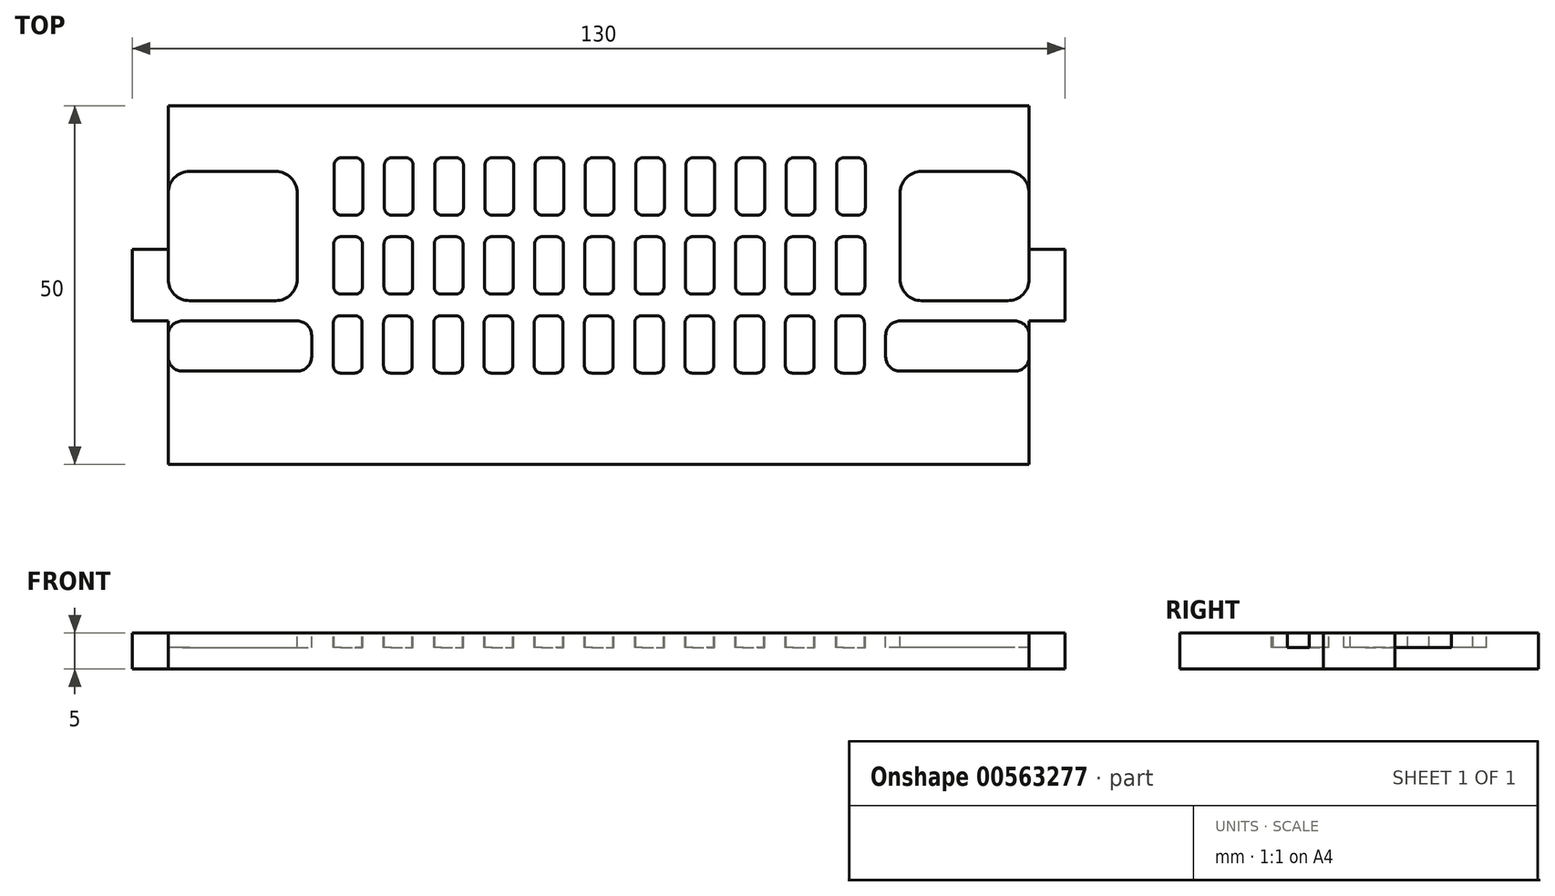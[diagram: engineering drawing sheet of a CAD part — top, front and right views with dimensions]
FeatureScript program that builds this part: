
annotation { "Feature Type Name" : "Feature", "Feature Type Description" : "" }
export const myFeature = defineFeature(function(context is Context, id is Id, definition is map)
    precondition{}
    {
        {
            var Q0;
            Q0=qCreatedBy(makeId("Top.planeOp"),FACE);
            var sketch = newSketch(context, id + "F0", { "sketchPlane" : qUnion([Q0])});
            skLineSegment(sketch, "E0.bottom", {"start": v(0, 0) * mm, "end": v(120, 0) * mm});
            skLineSegment(sketch, "E0.top", {"start": v(0, 50) * mm, "end": v(120, 50) * mm});
            skLineSegment(sketch, "E0.left", {"start": v(0, 0) * mm, "end": v(0, 20) * mm});
            skLineSegment(sketch, "E0.right", {"start": v(120, 0) * mm, "end": v(120, 20) * mm});
            skLineSegment(sketch, "E1.bottom", {"start": v(0, 30) * mm, "end": v(-5, 30) * mm});
            skLineSegment(sketch, "E1.top", {"start": v(0, 20) * mm, "end": v(-5, 20) * mm});
            skLineSegment(sketch, "E1.right", {"start": v(-5, 30) * mm, "end": v(-5, 20) * mm});
            skLineSegment(sketch, "E2.bottom", {"start": v(120, 30) * mm, "end": v(125, 30) * mm});
            skLineSegment(sketch, "E2.top", {"start": v(120, 20) * mm, "end": v(125, 20) * mm});
            skLineSegment(sketch, "E2.right", {"start": v(125, 30) * mm, "end": v(125, 20) * mm});
            skLineSegment(sketch, "E3.trimOffspring", {"start": v(0, 30) * mm, "end": v(0, 50) * mm});
            skLineSegment(sketch, "E4.trimOffspring", {"start": v(120, 30) * mm, "end": v(120, 50) * mm});
            skSolve(sketch);
        }
        {
            var Q0;
            Q0 = qSketchRegion(id + "F0", true);
            extrude(context, id + "F1", {"entities" : qUnion([Q0]), "depth" : 5 * mm, "offsetDistance" : 25 * mm});
        }
        {
            var Q0;
            Q0=makeQuery(id+"F1.opExtrude","CAP_FACE",FACE,{"disambiguationData":[OSD([sQuery(id+"F0.wireOp",EDGE,"E0.bottom"),sQuery(id+"F0.wireOp",EDGE,"E0.top"),sQuery(id+"F0.wireOp",EDGE,"E0.left"),sQuery(id+"F0.wireOp",EDGE,"E0.right"),sQuery(id+"F0.wireOp",EDGE,"E1.bottom"),sQuery(id+"F0.wireOp",EDGE,"E1.top"),sQuery(id+"F0.wireOp",EDGE,"E1.right"),sQuery(id+"F0.wireOp",EDGE,"E2.bottom"),sQuery(id+"F0.wireOp",EDGE,"E2.top"),sQuery(id+"F0.wireOp",EDGE,"E2.right"),sQuery(id+"F0.wireOp",EDGE,"E3.trimOffspring"),sQuery(id+"F0.wireOp",EDGE,"E4.trimOffspring")])],"isStart":false});
            var sketch = newSketch(context, id + "F2", { "sketchPlane" : qUnion([Q0])});
            skLineSegment(sketch, "E5.bottom", {"start": v(3, 40.83) * mm, "end": v(15, 40.83) * mm});
            skLineSegment(sketch, "E5.top", {"start": v(3, 22.83) * mm, "end": v(15, 22.83) * mm});
            skLineSegment(sketch, "E5.left", {"start": v(0, 37.83) * mm, "end": v(0, 25.83) * mm});
            skLineSegment(sketch, "E5.right", {"start": v(18, 37.83) * mm, "end": v(18, 25.83) * mm});
            skLineSegment(sketch, "E6.bottom", {"start": v(117, 40.83) * mm, "end": v(105, 40.83) * mm});
            skLineSegment(sketch, "E6.top", {"start": v(117, 22.83) * mm, "end": v(105, 22.83) * mm});
            skLineSegment(sketch, "E6.left", {"start": v(120, 37.83) * mm, "end": v(120, 25.83) * mm});
            skLineSegment(sketch, "E6.right", {"start": v(102, 37.83) * mm, "end": v(102, 25.83) * mm});
            skPoint(sketch, "E7.visualSharp", {"position": v(0, 40.83) * mm});
            skArc(sketch, "E7.filletArc", {"start": v(3, 40.83) * mm, "mid": v(0.88, 39.95) * mm, "end": v(0, 37.83) * mm});
            skPoint(sketch, "E8.visualSharp", {"position": v(18, 40.83) * mm});
            skArc(sketch, "E8.filletArc", {"start": v(18, 37.83) * mm, "mid": v(17.12, 39.95) * mm, "end": v(15, 40.83) * mm});
            skPoint(sketch, "E9.visualSharp", {"position": v(0, 22.83) * mm});
            skArc(sketch, "E9.filletArc", {"start": v(0, 25.83) * mm, "mid": v(0.88, 23.7) * mm, "end": v(3, 22.83) * mm});
            skPoint(sketch, "E10.visualSharp", {"position": v(102, 22.83) * mm});
            skArc(sketch, "E10.filletArc", {"start": v(102, 25.83) * mm, "mid": v(102.88, 23.7) * mm, "end": v(105, 22.83) * mm});
            skPoint(sketch, "E11.visualSharp", {"position": v(120, 40.83) * mm});
            skArc(sketch, "E11.filletArc", {"start": v(120, 37.83) * mm, "mid": v(119.12, 39.95) * mm, "end": v(117, 40.83) * mm});
            skPoint(sketch, "E12.visualSharp", {"position": v(102, 40.83) * mm});
            skArc(sketch, "E12.filletArc", {"start": v(105, 40.83) * mm, "mid": v(102.88, 39.95) * mm, "end": v(102, 37.83) * mm});
            skPoint(sketch, "E13.visualSharp", {"position": v(18, 22.83) * mm});
            skArc(sketch, "E13.filletArc", {"start": v(15, 22.83) * mm, "mid": v(17.12, 23.7) * mm, "end": v(18, 25.83) * mm});
            skPoint(sketch, "E14.visualSharp", {"position": v(120, 22.83) * mm});
            skArc(sketch, "E14.filletArc", {"start": v(117, 22.83) * mm, "mid": v(119.12, 23.7) * mm, "end": v(120, 25.83) * mm});
            skLineSegment(sketch, "E15.bottom", {"start": v(2, 20) * mm, "end": v(18, 20) * mm});
            skLineSegment(sketch, "E15.top", {"start": v(2, 13) * mm, "end": v(18, 13) * mm});
            skLineSegment(sketch, "E15.left", {"start": v(0, 18) * mm, "end": v(0, 15) * mm});
            skLineSegment(sketch, "E15.right", {"start": v(20, 18) * mm, "end": v(20, 15) * mm});
            skLineSegment(sketch, "E16.bottom", {"start": v(118, 20) * mm, "end": v(102, 20) * mm});
            skLineSegment(sketch, "E16.top", {"start": v(118, 13) * mm, "end": v(102, 13) * mm});
            skLineSegment(sketch, "E16.left", {"start": v(120, 18) * mm, "end": v(120, 15) * mm});
            skLineSegment(sketch, "E16.right", {"start": v(100, 18) * mm, "end": v(100, 15) * mm});
            skPoint(sketch, "E17.visualSharp", {"position": v(20, 20) * mm});
            skArc(sketch, "E17.filletArc", {"start": v(20, 18) * mm, "mid": v(19.41, 19.41) * mm, "end": v(18, 20) * mm});
            skPoint(sketch, "E18.visualSharp", {"position": v(0, 20) * mm});
            skArc(sketch, "E18.filletArc", {"start": v(2, 20) * mm, "mid": v(0.59, 19.41) * mm, "end": v(0, 18) * mm});
            skPoint(sketch, "E19.visualSharp", {"position": v(20, 13) * mm});
            skArc(sketch, "E19.filletArc", {"start": v(18, 13) * mm, "mid": v(19.41, 13.59) * mm, "end": v(20, 15) * mm});
            skPoint(sketch, "E20.visualSharp", {"position": v(100, 13) * mm});
            skArc(sketch, "E20.filletArc", {"start": v(100, 15) * mm, "mid": v(100.59, 13.59) * mm, "end": v(102, 13) * mm});
            skPoint(sketch, "E21.visualSharp", {"position": v(120, 20) * mm});
            skArc(sketch, "E21.filletArc", {"start": v(120, 18) * mm, "mid": v(119.41, 19.41) * mm, "end": v(118, 20) * mm});
            skPoint(sketch, "E22.visualSharp", {"position": v(100, 20) * mm});
            skArc(sketch, "E22.filletArc", {"start": v(102, 20) * mm, "mid": v(100.59, 19.41) * mm, "end": v(100, 18) * mm});
            skPoint(sketch, "E23.visualSharp", {"position": v(120, 13) * mm});
            skArc(sketch, "E23.filletArc", {"start": v(118, 13) * mm, "mid": v(119.41, 13.59) * mm, "end": v(120, 15) * mm});
            skPoint(sketch, "E24.visualSharp", {"position": v(0, 13) * mm});
            skArc(sketch, "E24.filletArc", {"start": v(0, 15) * mm, "mid": v(0.59, 13.59) * mm, "end": v(2, 13) * mm});
            skLineSegment(sketch, "E25.bottom", {"start": v(24.15, 42.74) * mm, "end": v(26.15, 42.74) * mm});
            skLineSegment(sketch, "E25.top", {"start": v(24.15, 34.74) * mm, "end": v(26.15, 34.74) * mm});
            skLineSegment(sketch, "E25.left", {"start": v(23.15, 41.74) * mm, "end": v(23.15, 35.74) * mm});
            skLineSegment(sketch, "E25.right", {"start": v(27.15, 41.74) * mm, "end": v(27.15, 35.74) * mm});
            skPoint(sketch, "E26.visualSharp", {"position": v(27.15, 42.74) * mm});
            skArc(sketch, "E26.filletArc", {"start": v(27.15, 41.74) * mm, "mid": v(26.86, 42.45) * mm, "end": v(26.15, 42.74) * mm});
            skPoint(sketch, "E27.visualSharp", {"position": v(23.15, 42.74) * mm});
            skArc(sketch, "E27.filletArc", {"start": v(24.15, 42.74) * mm, "mid": v(23.44, 42.45) * mm, "end": v(23.15, 41.74) * mm});
            skPoint(sketch, "E28.visualSharp", {"position": v(27.15, 34.74) * mm});
            skArc(sketch, "E28.filletArc", {"start": v(26.15, 34.74) * mm, "mid": v(26.86, 35.03) * mm, "end": v(27.15, 35.74) * mm});
            skPoint(sketch, "E29.visualSharp", {"position": v(23.15, 34.74) * mm});
            skArc(sketch, "E29.filletArc", {"start": v(23.15, 35.74) * mm, "mid": v(23.44, 35.03) * mm, "end": v(24.15, 34.74) * mm});
            skLineSegment(sketch, "E30.direction1", {"start": v(23.15, 34.74) * mm, "end": v(26.15, 34.74) * mm, "construction": true});
            skLineSegment(sketch, "E31.1.0.0", {"start": v(31.15, 42.74) * mm, "end": v(33.15, 42.74) * mm});
            skPoint(sketch, "E31.1.0.1", {"position": v(34.15, 42.74) * mm});
            skLineSegment(sketch, "E31.1.0.2", {"start": v(30.15, 34.74) * mm, "end": v(33.15, 34.74) * mm, "construction": true});
            skPoint(sketch, "E31.1.0.3", {"position": v(30.15, 42.74) * mm});
            skLineSegment(sketch, "E31.1.0.4", {"start": v(34.15, 41.74) * mm, "end": v(34.15, 35.74) * mm});
            skLineSegment(sketch, "E31.1.0.5", {"start": v(30.15, 41.74) * mm, "end": v(30.15, 35.74) * mm});
            skPoint(sketch, "E31.1.0.6", {"position": v(30.15, 34.74) * mm});
            skPoint(sketch, "E31.1.0.7", {"position": v(34.15, 34.74) * mm});
            skArc(sketch, "E31.1.0.8", {"start": v(34.15, 41.74) * mm, "mid": v(33.86, 42.45) * mm, "end": v(33.15, 42.74) * mm});
            skArc(sketch, "E31.1.0.9", {"start": v(31.15, 42.74) * mm, "mid": v(30.44, 42.45) * mm, "end": v(30.15, 41.74) * mm});
            skArc(sketch, "E31.1.0.10", {"start": v(30.15, 35.74) * mm, "mid": v(30.44, 35.03) * mm, "end": v(31.15, 34.74) * mm});
            skArc(sketch, "E31.1.0.11", {"start": v(33.15, 34.74) * mm, "mid": v(33.86, 35.03) * mm, "end": v(34.15, 35.74) * mm});
            skLineSegment(sketch, "E31.1.0.12", {"start": v(31.15, 34.74) * mm, "end": v(33.15, 34.74) * mm});
            skLineSegment(sketch, "E31.2.0.0", {"start": v(38.15, 42.74) * mm, "end": v(40.15, 42.74) * mm});
            skPoint(sketch, "E31.2.0.1", {"position": v(41.15, 42.74) * mm});
            skLineSegment(sketch, "E31.2.0.2", {"start": v(37.15, 34.74) * mm, "end": v(40.15, 34.74) * mm, "construction": true});
            skPoint(sketch, "E31.2.0.3", {"position": v(37.15, 42.74) * mm});
            skLineSegment(sketch, "E31.2.0.4", {"start": v(41.15, 41.74) * mm, "end": v(41.15, 35.74) * mm});
            skLineSegment(sketch, "E31.2.0.5", {"start": v(37.15, 41.74) * mm, "end": v(37.15, 35.74) * mm});
            skPoint(sketch, "E31.2.0.6", {"position": v(37.15, 34.74) * mm});
            skPoint(sketch, "E31.2.0.7", {"position": v(41.15, 34.74) * mm});
            skArc(sketch, "E31.2.0.8", {"start": v(41.15, 41.74) * mm, "mid": v(40.86, 42.45) * mm, "end": v(40.15, 42.74) * mm});
            skArc(sketch, "E31.2.0.9", {"start": v(38.15, 42.74) * mm, "mid": v(37.44, 42.45) * mm, "end": v(37.15, 41.74) * mm});
            skArc(sketch, "E31.2.0.10", {"start": v(37.15, 35.74) * mm, "mid": v(37.44, 35.03) * mm, "end": v(38.15, 34.74) * mm});
            skArc(sketch, "E31.2.0.11", {"start": v(40.15, 34.74) * mm, "mid": v(40.86, 35.03) * mm, "end": v(41.15, 35.74) * mm});
            skLineSegment(sketch, "E31.2.0.12", {"start": v(38.15, 34.74) * mm, "end": v(40.15, 34.74) * mm});
            skLineSegment(sketch, "E31.3.0.0", {"start": v(45.15, 42.74) * mm, "end": v(47.15, 42.74) * mm});
            skPoint(sketch, "E31.3.0.1", {"position": v(48.15, 42.74) * mm});
            skLineSegment(sketch, "E31.3.0.2", {"start": v(44.15, 34.74) * mm, "end": v(47.15, 34.74) * mm, "construction": true});
            skPoint(sketch, "E31.3.0.3", {"position": v(44.15, 42.74) * mm});
            skLineSegment(sketch, "E31.3.0.4", {"start": v(48.15, 41.74) * mm, "end": v(48.15, 35.74) * mm});
            skLineSegment(sketch, "E31.3.0.5", {"start": v(44.15, 41.74) * mm, "end": v(44.15, 35.74) * mm});
            skPoint(sketch, "E31.3.0.6", {"position": v(44.15, 34.74) * mm});
            skPoint(sketch, "E31.3.0.7", {"position": v(48.15, 34.74) * mm});
            skArc(sketch, "E31.3.0.8", {"start": v(48.15, 41.74) * mm, "mid": v(47.86, 42.45) * mm, "end": v(47.15, 42.74) * mm});
            skArc(sketch, "E31.3.0.9", {"start": v(45.15, 42.74) * mm, "mid": v(44.44, 42.45) * mm, "end": v(44.15, 41.74) * mm});
            skArc(sketch, "E31.3.0.10", {"start": v(44.15, 35.74) * mm, "mid": v(44.44, 35.03) * mm, "end": v(45.15, 34.74) * mm});
            skArc(sketch, "E31.3.0.11", {"start": v(47.15, 34.74) * mm, "mid": v(47.86, 35.03) * mm, "end": v(48.15, 35.74) * mm});
            skLineSegment(sketch, "E31.3.0.12", {"start": v(45.15, 34.74) * mm, "end": v(47.15, 34.74) * mm});
            skLineSegment(sketch, "E31.4.0.0", {"start": v(52.15, 42.74) * mm, "end": v(54.15, 42.74) * mm});
            skPoint(sketch, "E31.4.0.1", {"position": v(55.15, 42.74) * mm});
            skLineSegment(sketch, "E31.4.0.2", {"start": v(51.15, 34.74) * mm, "end": v(54.15, 34.74) * mm, "construction": true});
            skPoint(sketch, "E31.4.0.3", {"position": v(51.15, 42.74) * mm});
            skLineSegment(sketch, "E31.4.0.4", {"start": v(55.15, 41.74) * mm, "end": v(55.15, 35.74) * mm});
            skLineSegment(sketch, "E31.4.0.5", {"start": v(51.15, 41.74) * mm, "end": v(51.15, 35.74) * mm});
            skPoint(sketch, "E31.4.0.6", {"position": v(51.15, 34.74) * mm});
            skPoint(sketch, "E31.4.0.7", {"position": v(55.15, 34.74) * mm});
            skArc(sketch, "E31.4.0.8", {"start": v(55.15, 41.74) * mm, "mid": v(54.86, 42.45) * mm, "end": v(54.15, 42.74) * mm});
            skArc(sketch, "E31.4.0.9", {"start": v(52.15, 42.74) * mm, "mid": v(51.44, 42.45) * mm, "end": v(51.15, 41.74) * mm});
            skArc(sketch, "E31.4.0.10", {"start": v(51.15, 35.74) * mm, "mid": v(51.44, 35.03) * mm, "end": v(52.15, 34.74) * mm});
            skArc(sketch, "E31.4.0.11", {"start": v(54.15, 34.74) * mm, "mid": v(54.86, 35.03) * mm, "end": v(55.15, 35.74) * mm});
            skLineSegment(sketch, "E31.4.0.12", {"start": v(52.15, 34.74) * mm, "end": v(54.15, 34.74) * mm});
            skLineSegment(sketch, "E31.5.0.0", {"start": v(59.15, 42.74) * mm, "end": v(61.15, 42.74) * mm});
            skPoint(sketch, "E31.5.0.1", {"position": v(62.15, 42.74) * mm});
            skLineSegment(sketch, "E31.5.0.2", {"start": v(58.15, 34.74) * mm, "end": v(61.15, 34.74) * mm, "construction": true});
            skPoint(sketch, "E31.5.0.3", {"position": v(58.15, 42.74) * mm});
            skLineSegment(sketch, "E31.5.0.4", {"start": v(62.15, 41.74) * mm, "end": v(62.15, 35.74) * mm});
            skLineSegment(sketch, "E31.5.0.5", {"start": v(58.15, 41.74) * mm, "end": v(58.15, 35.74) * mm});
            skPoint(sketch, "E31.5.0.6", {"position": v(58.15, 34.74) * mm});
            skPoint(sketch, "E31.5.0.7", {"position": v(62.15, 34.74) * mm});
            skArc(sketch, "E31.5.0.8", {"start": v(62.15, 41.74) * mm, "mid": v(61.86, 42.45) * mm, "end": v(61.15, 42.74) * mm});
            skArc(sketch, "E31.5.0.9", {"start": v(59.15, 42.74) * mm, "mid": v(58.44, 42.45) * mm, "end": v(58.15, 41.74) * mm});
            skArc(sketch, "E31.5.0.10", {"start": v(58.15, 35.74) * mm, "mid": v(58.44, 35.03) * mm, "end": v(59.15, 34.74) * mm});
            skArc(sketch, "E31.5.0.11", {"start": v(61.15, 34.74) * mm, "mid": v(61.86, 35.03) * mm, "end": v(62.15, 35.74) * mm});
            skLineSegment(sketch, "E31.5.0.12", {"start": v(59.15, 34.74) * mm, "end": v(61.15, 34.74) * mm});
            skLineSegment(sketch, "E31.6.0.0", {"start": v(66.15, 42.74) * mm, "end": v(68.15, 42.74) * mm});
            skPoint(sketch, "E31.6.0.1", {"position": v(69.15, 42.74) * mm});
            skLineSegment(sketch, "E31.6.0.2", {"start": v(65.15, 34.74) * mm, "end": v(68.15, 34.74) * mm, "construction": true});
            skPoint(sketch, "E31.6.0.3", {"position": v(65.15, 42.74) * mm});
            skLineSegment(sketch, "E31.6.0.4", {"start": v(69.15, 41.74) * mm, "end": v(69.15, 35.74) * mm});
            skLineSegment(sketch, "E31.6.0.5", {"start": v(65.15, 41.74) * mm, "end": v(65.15, 35.74) * mm});
            skPoint(sketch, "E31.6.0.6", {"position": v(65.15, 34.74) * mm});
            skPoint(sketch, "E31.6.0.7", {"position": v(69.15, 34.74) * mm});
            skArc(sketch, "E31.6.0.8", {"start": v(69.15, 41.74) * mm, "mid": v(68.86, 42.45) * mm, "end": v(68.15, 42.74) * mm});
            skArc(sketch, "E31.6.0.9", {"start": v(66.15, 42.74) * mm, "mid": v(65.44, 42.45) * mm, "end": v(65.15, 41.74) * mm});
            skArc(sketch, "E31.6.0.10", {"start": v(65.15, 35.74) * mm, "mid": v(65.44, 35.03) * mm, "end": v(66.15, 34.74) * mm});
            skArc(sketch, "E31.6.0.11", {"start": v(68.15, 34.74) * mm, "mid": v(68.86, 35.03) * mm, "end": v(69.15, 35.74) * mm});
            skLineSegment(sketch, "E31.6.0.12", {"start": v(66.15, 34.74) * mm, "end": v(68.15, 34.74) * mm});
            skLineSegment(sketch, "E31.7.0.0", {"start": v(73.15, 42.74) * mm, "end": v(75.15, 42.74) * mm});
            skPoint(sketch, "E31.7.0.1", {"position": v(76.15, 42.74) * mm});
            skLineSegment(sketch, "E31.7.0.2", {"start": v(72.15, 34.74) * mm, "end": v(75.15, 34.74) * mm, "construction": true});
            skPoint(sketch, "E31.7.0.3", {"position": v(72.15, 42.74) * mm});
            skLineSegment(sketch, "E31.7.0.4", {"start": v(76.15, 41.74) * mm, "end": v(76.15, 35.74) * mm});
            skLineSegment(sketch, "E31.7.0.5", {"start": v(72.15, 41.74) * mm, "end": v(72.15, 35.74) * mm});
            skPoint(sketch, "E31.7.0.6", {"position": v(72.15, 34.74) * mm});
            skPoint(sketch, "E31.7.0.7", {"position": v(76.15, 34.74) * mm});
            skArc(sketch, "E31.7.0.8", {"start": v(76.15, 41.74) * mm, "mid": v(75.86, 42.45) * mm, "end": v(75.15, 42.74) * mm});
            skArc(sketch, "E31.7.0.9", {"start": v(73.15, 42.74) * mm, "mid": v(72.44, 42.45) * mm, "end": v(72.15, 41.74) * mm});
            skArc(sketch, "E31.7.0.10", {"start": v(72.15, 35.74) * mm, "mid": v(72.44, 35.03) * mm, "end": v(73.15, 34.74) * mm});
            skArc(sketch, "E31.7.0.11", {"start": v(75.15, 34.74) * mm, "mid": v(75.86, 35.03) * mm, "end": v(76.15, 35.74) * mm});
            skLineSegment(sketch, "E31.7.0.12", {"start": v(73.15, 34.74) * mm, "end": v(75.15, 34.74) * mm});
            skLineSegment(sketch, "E31.8.0.0", {"start": v(80.15, 42.74) * mm, "end": v(82.15, 42.74) * mm});
            skPoint(sketch, "E31.8.0.1", {"position": v(83.15, 42.74) * mm});
            skLineSegment(sketch, "E31.8.0.2", {"start": v(79.15, 34.74) * mm, "end": v(82.15, 34.74) * mm, "construction": true});
            skPoint(sketch, "E31.8.0.3", {"position": v(79.15, 42.74) * mm});
            skLineSegment(sketch, "E31.8.0.4", {"start": v(83.15, 41.74) * mm, "end": v(83.15, 35.74) * mm});
            skLineSegment(sketch, "E31.8.0.5", {"start": v(79.15, 41.74) * mm, "end": v(79.15, 35.74) * mm});
            skPoint(sketch, "E31.8.0.6", {"position": v(79.15, 34.74) * mm});
            skPoint(sketch, "E31.8.0.7", {"position": v(83.15, 34.74) * mm});
            skArc(sketch, "E31.8.0.8", {"start": v(83.15, 41.74) * mm, "mid": v(82.86, 42.45) * mm, "end": v(82.15, 42.74) * mm});
            skArc(sketch, "E31.8.0.9", {"start": v(80.15, 42.74) * mm, "mid": v(79.44, 42.45) * mm, "end": v(79.15, 41.74) * mm});
            skArc(sketch, "E31.8.0.10", {"start": v(79.15, 35.74) * mm, "mid": v(79.44, 35.03) * mm, "end": v(80.15, 34.74) * mm});
            skArc(sketch, "E31.8.0.11", {"start": v(82.15, 34.74) * mm, "mid": v(82.86, 35.03) * mm, "end": v(83.15, 35.74) * mm});
            skLineSegment(sketch, "E31.8.0.12", {"start": v(80.15, 34.74) * mm, "end": v(82.15, 34.74) * mm});
            skLineSegment(sketch, "E31.9.0.0", {"start": v(87.15, 42.74) * mm, "end": v(89.15, 42.74) * mm});
            skPoint(sketch, "E31.9.0.1", {"position": v(90.15, 42.74) * mm});
            skLineSegment(sketch, "E31.9.0.2", {"start": v(86.15, 34.74) * mm, "end": v(89.15, 34.74) * mm, "construction": true});
            skPoint(sketch, "E31.9.0.3", {"position": v(86.15, 42.74) * mm});
            skLineSegment(sketch, "E31.9.0.4", {"start": v(90.15, 41.74) * mm, "end": v(90.15, 35.74) * mm});
            skLineSegment(sketch, "E31.9.0.5", {"start": v(86.15, 41.74) * mm, "end": v(86.15, 35.74) * mm});
            skPoint(sketch, "E31.9.0.6", {"position": v(86.15, 34.74) * mm});
            skPoint(sketch, "E31.9.0.7", {"position": v(90.15, 34.74) * mm});
            skArc(sketch, "E31.9.0.8", {"start": v(90.15, 41.74) * mm, "mid": v(89.86, 42.45) * mm, "end": v(89.15, 42.74) * mm});
            skArc(sketch, "E31.9.0.9", {"start": v(87.15, 42.74) * mm, "mid": v(86.44, 42.45) * mm, "end": v(86.15, 41.74) * mm});
            skArc(sketch, "E31.9.0.10", {"start": v(86.15, 35.74) * mm, "mid": v(86.44, 35.03) * mm, "end": v(87.15, 34.74) * mm});
            skArc(sketch, "E31.9.0.11", {"start": v(89.15, 34.74) * mm, "mid": v(89.86, 35.03) * mm, "end": v(90.15, 35.74) * mm});
            skLineSegment(sketch, "E31.9.0.12", {"start": v(87.15, 34.74) * mm, "end": v(89.15, 34.74) * mm});
            skLineSegment(sketch, "E31.10.0.0", {"start": v(94.15, 42.74) * mm, "end": v(96.15, 42.74) * mm});
            skPoint(sketch, "E31.10.0.1", {"position": v(97.15, 42.74) * mm});
            skLineSegment(sketch, "E31.10.0.2", {"start": v(93.15, 34.74) * mm, "end": v(96.15, 34.74) * mm, "construction": true});
            skPoint(sketch, "E31.10.0.3", {"position": v(93.15, 42.74) * mm});
            skLineSegment(sketch, "E31.10.0.4", {"start": v(97.15, 41.74) * mm, "end": v(97.15, 35.74) * mm});
            skLineSegment(sketch, "E31.10.0.5", {"start": v(93.15, 41.74) * mm, "end": v(93.15, 35.74) * mm});
            skPoint(sketch, "E31.10.0.6", {"position": v(93.15, 34.74) * mm});
            skPoint(sketch, "E31.10.0.7", {"position": v(97.15, 34.74) * mm});
            skArc(sketch, "E31.10.0.8", {"start": v(97.15, 41.74) * mm, "mid": v(96.86, 42.45) * mm, "end": v(96.15, 42.74) * mm});
            skArc(sketch, "E31.10.0.9", {"start": v(94.15, 42.74) * mm, "mid": v(93.44, 42.45) * mm, "end": v(93.15, 41.74) * mm});
            skArc(sketch, "E31.10.0.10", {"start": v(93.15, 35.74) * mm, "mid": v(93.44, 35.03) * mm, "end": v(94.15, 34.74) * mm});
            skArc(sketch, "E31.10.0.11", {"start": v(96.15, 34.74) * mm, "mid": v(96.86, 35.03) * mm, "end": v(97.15, 35.74) * mm});
            skLineSegment(sketch, "E31.10.0.12", {"start": v(94.15, 34.74) * mm, "end": v(96.15, 34.74) * mm});
            skLineSegment(sketch, "E31.direction1", {"start": v(23.15, 34.74) * mm, "end": v(30.15, 34.74) * mm, "construction": true});
            skPoint(sketch, "E32.1.0.0", {"position": v(97.09, 23.74) * mm});
            skPoint(sketch, "E32.1.0.1", {"position": v(44.09, 31.74) * mm});
            skPoint(sketch, "E32.1.0.2", {"position": v(30.09, 31.74) * mm});
            skLineSegment(sketch, "E32.1.0.3", {"start": v(34.09, 30.74) * mm, "end": v(34.09, 24.74) * mm});
            skPoint(sketch, "E32.1.0.4", {"position": v(41.09, 31.74) * mm});
            skPoint(sketch, "E32.1.0.5", {"position": v(37.09, 31.74) * mm});
            skPoint(sketch, "E32.1.0.6", {"position": v(27.09, 23.74) * mm});
            skLineSegment(sketch, "E32.1.0.7", {"start": v(93.09, 30.74) * mm, "end": v(93.09, 24.74) * mm});
            skPoint(sketch, "E32.1.0.8", {"position": v(76.09, 31.74) * mm});
            skPoint(sketch, "E32.1.0.9", {"position": v(86.09, 31.74) * mm});
            skLineSegment(sketch, "E32.1.0.10", {"start": v(79.09, 30.74) * mm, "end": v(79.09, 24.74) * mm});
            skPoint(sketch, "E32.1.0.11", {"position": v(27.09, 31.74) * mm});
            skPoint(sketch, "E32.1.0.12", {"position": v(72.09, 31.74) * mm});
            skLineSegment(sketch, "E32.1.0.13", {"start": v(69.09, 30.74) * mm, "end": v(69.09, 24.74) * mm});
            skLineSegment(sketch, "E32.1.0.14", {"start": v(76.09, 30.74) * mm, "end": v(76.09, 24.74) * mm});
            skPoint(sketch, "E32.1.0.15", {"position": v(58.09, 31.74) * mm});
            skPoint(sketch, "E32.1.0.16", {"position": v(41.09, 23.74) * mm});
            skPoint(sketch, "E32.1.0.17", {"position": v(55.09, 31.74) * mm});
            skPoint(sketch, "E32.1.0.18", {"position": v(69.09, 31.74) * mm});
            skPoint(sketch, "E32.1.0.19", {"position": v(83.09, 31.74) * mm});
            skPoint(sketch, "E32.1.0.20", {"position": v(69.09, 23.74) * mm});
            skPoint(sketch, "E32.1.0.21", {"position": v(97.09, 31.74) * mm});
            skLineSegment(sketch, "E32.1.0.22", {"start": v(51.09, 30.74) * mm, "end": v(51.09, 24.74) * mm});
            skLineSegment(sketch, "E32.1.0.23", {"start": v(55.09, 30.74) * mm, "end": v(55.09, 24.74) * mm});
            skLineSegment(sketch, "E32.1.0.24", {"start": v(37.09, 30.74) * mm, "end": v(37.09, 24.74) * mm});
            skLineSegment(sketch, "E32.1.0.25", {"start": v(44.09, 30.74) * mm, "end": v(44.09, 24.74) * mm});
            skLineSegment(sketch, "E32.1.0.26", {"start": v(86.09, 30.74) * mm, "end": v(86.09, 24.74) * mm});
            skLineSegment(sketch, "E32.1.0.27", {"start": v(41.09, 30.74) * mm, "end": v(41.09, 24.74) * mm});
            skLineSegment(sketch, "E32.1.0.28", {"start": v(65.09, 30.74) * mm, "end": v(65.09, 24.74) * mm});
            skLineSegment(sketch, "E32.1.0.29", {"start": v(90.09, 30.74) * mm, "end": v(90.09, 24.74) * mm});
            skLineSegment(sketch, "E32.1.0.30", {"start": v(27.09, 30.74) * mm, "end": v(27.09, 24.74) * mm});
            skPoint(sketch, "E32.1.0.31", {"position": v(76.09, 23.74) * mm});
            skPoint(sketch, "E32.1.0.32", {"position": v(90.09, 23.74) * mm});
            skPoint(sketch, "E32.1.0.33", {"position": v(34.09, 23.74) * mm});
            skPoint(sketch, "E32.1.0.34", {"position": v(48.09, 23.74) * mm});
            skPoint(sketch, "E32.1.0.35", {"position": v(62.09, 23.74) * mm});
            skPoint(sketch, "E32.1.0.36", {"position": v(83.09, 23.74) * mm});
            skLineSegment(sketch, "E32.1.0.37", {"start": v(72.09, 30.74) * mm, "end": v(72.09, 24.74) * mm});
            skLineSegment(sketch, "E32.1.0.38", {"start": v(23.09, 30.74) * mm, "end": v(23.09, 24.74) * mm});
            skPoint(sketch, "E32.1.0.39", {"position": v(72.09, 23.74) * mm});
            skPoint(sketch, "E32.1.0.40", {"position": v(86.09, 23.74) * mm});
            skPoint(sketch, "E32.1.0.41", {"position": v(30.09, 23.74) * mm});
            skPoint(sketch, "E32.1.0.42", {"position": v(44.09, 23.74) * mm});
            skPoint(sketch, "E32.1.0.43", {"position": v(58.09, 23.74) * mm});
            skPoint(sketch, "E32.1.0.44", {"position": v(90.09, 31.74) * mm});
            skPoint(sketch, "E32.1.0.45", {"position": v(51.09, 31.74) * mm});
            skPoint(sketch, "E32.1.0.46", {"position": v(55.09, 23.74) * mm});
            skPoint(sketch, "E32.1.0.47", {"position": v(34.09, 31.74) * mm});
            skLineSegment(sketch, "E32.1.0.48", {"start": v(97.09, 30.74) * mm, "end": v(97.09, 24.74) * mm});
            skPoint(sketch, "E32.1.0.49", {"position": v(23.09, 23.74) * mm});
            skLineSegment(sketch, "E32.1.0.50", {"start": v(48.09, 30.74) * mm, "end": v(48.09, 24.74) * mm});
            skPoint(sketch, "E32.1.0.51", {"position": v(65.09, 31.74) * mm});
            skLineSegment(sketch, "E32.1.0.52", {"start": v(83.09, 30.74) * mm, "end": v(83.09, 24.74) * mm});
            skPoint(sketch, "E32.1.0.53", {"position": v(79.09, 31.74) * mm});
            skPoint(sketch, "E32.1.0.54", {"position": v(48.09, 31.74) * mm});
            skPoint(sketch, "E32.1.0.55", {"position": v(62.09, 31.74) * mm});
            skLineSegment(sketch, "E32.1.0.56", {"start": v(62.09, 30.74) * mm, "end": v(62.09, 24.74) * mm});
            skPoint(sketch, "E32.1.0.57", {"position": v(51.09, 23.74) * mm});
            skLineSegment(sketch, "E32.1.0.58", {"start": v(30.09, 30.74) * mm, "end": v(30.09, 24.74) * mm});
            skPoint(sketch, "E32.1.0.59", {"position": v(93.09, 31.74) * mm});
            skPoint(sketch, "E32.1.0.60", {"position": v(65.09, 23.74) * mm});
            skPoint(sketch, "E32.1.0.61", {"position": v(79.09, 23.74) * mm});
            skPoint(sketch, "E32.1.0.62", {"position": v(93.09, 23.74) * mm});
            skPoint(sketch, "E32.1.0.63", {"position": v(23.09, 31.74) * mm});
            skPoint(sketch, "E32.1.0.64", {"position": v(37.09, 23.74) * mm});
            skLineSegment(sketch, "E32.1.0.65", {"start": v(58.09, 30.74) * mm, "end": v(58.09, 24.74) * mm});
            skLineSegment(sketch, "E32.1.0.66", {"start": v(23.09, 23.74) * mm, "end": v(30.09, 23.74) * mm, "construction": true});
            skArc(sketch, "E32.1.0.67", {"start": v(66.09, 31.74) * mm, "mid": v(65.38, 31.45) * mm, "end": v(65.09, 30.74) * mm});
            skArc(sketch, "E32.1.0.68", {"start": v(83.09, 30.74) * mm, "mid": v(82.8, 31.45) * mm, "end": v(82.09, 31.74) * mm});
            skArc(sketch, "E32.1.0.69", {"start": v(65.09, 24.74) * mm, "mid": v(65.38, 24.03) * mm, "end": v(66.09, 23.74) * mm});
            skLineSegment(sketch, "E32.1.0.70", {"start": v(45.09, 31.74) * mm, "end": v(47.09, 31.74) * mm});
            skArc(sketch, "E32.1.0.71", {"start": v(94.09, 31.74) * mm, "mid": v(93.38, 31.45) * mm, "end": v(93.09, 30.74) * mm});
            skLineSegment(sketch, "E32.1.0.72", {"start": v(80.09, 31.74) * mm, "end": v(82.09, 31.74) * mm});
            skLineSegment(sketch, "E32.1.0.73", {"start": v(65.09, 23.74) * mm, "end": v(68.09, 23.74) * mm, "construction": true});
            skArc(sketch, "E32.1.0.74", {"start": v(62.09, 30.74) * mm, "mid": v(61.8, 31.45) * mm, "end": v(61.09, 31.74) * mm});
            skLineSegment(sketch, "E32.1.0.75", {"start": v(87.09, 31.74) * mm, "end": v(89.09, 31.74) * mm});
            skArc(sketch, "E32.1.0.76", {"start": v(55.09, 30.74) * mm, "mid": v(54.8, 31.45) * mm, "end": v(54.09, 31.74) * mm});
            skArc(sketch, "E32.1.0.77", {"start": v(34.09, 30.74) * mm, "mid": v(33.8, 31.45) * mm, "end": v(33.09, 31.74) * mm});
            skArc(sketch, "E32.1.0.78", {"start": v(38.09, 31.74) * mm, "mid": v(37.38, 31.45) * mm, "end": v(37.09, 30.74) * mm});
            skArc(sketch, "E32.1.0.79", {"start": v(87.09, 31.74) * mm, "mid": v(86.38, 31.45) * mm, "end": v(86.09, 30.74) * mm});
            skArc(sketch, "E32.1.0.80", {"start": v(41.09, 30.74) * mm, "mid": v(40.8, 31.45) * mm, "end": v(40.09, 31.74) * mm});
            skLineSegment(sketch, "E32.1.0.81", {"start": v(66.09, 31.74) * mm, "end": v(68.09, 31.74) * mm});
            skArc(sketch, "E32.1.0.82", {"start": v(31.09, 31.74) * mm, "mid": v(30.38, 31.45) * mm, "end": v(30.09, 30.74) * mm});
            skArc(sketch, "E32.1.0.83", {"start": v(90.09, 30.74) * mm, "mid": v(89.8, 31.45) * mm, "end": v(89.09, 31.74) * mm});
            skLineSegment(sketch, "E32.1.0.84", {"start": v(59.09, 23.74) * mm, "end": v(61.09, 23.74) * mm});
            skArc(sketch, "E32.1.0.85", {"start": v(24.09, 31.74) * mm, "mid": v(23.38, 31.45) * mm, "end": v(23.09, 30.74) * mm});
            skLineSegment(sketch, "E32.1.0.86", {"start": v(58.09, 23.74) * mm, "end": v(61.09, 23.74) * mm, "construction": true});
            skLineSegment(sketch, "E32.1.0.87", {"start": v(52.09, 31.74) * mm, "end": v(54.09, 31.74) * mm});
            skArc(sketch, "E32.1.0.88", {"start": v(73.09, 31.74) * mm, "mid": v(72.38, 31.45) * mm, "end": v(72.09, 30.74) * mm});
            skArc(sketch, "E32.1.0.89", {"start": v(27.09, 30.74) * mm, "mid": v(26.8, 31.45) * mm, "end": v(26.09, 31.74) * mm});
            skLineSegment(sketch, "E32.1.0.90", {"start": v(79.09, 23.74) * mm, "end": v(82.09, 23.74) * mm, "construction": true});
            skArc(sketch, "E32.1.0.91", {"start": v(58.09, 24.74) * mm, "mid": v(58.38, 24.03) * mm, "end": v(59.09, 23.74) * mm});
            skArc(sketch, "E32.1.0.92", {"start": v(76.09, 30.74) * mm, "mid": v(75.8, 31.45) * mm, "end": v(75.09, 31.74) * mm});
            skLineSegment(sketch, "E32.1.0.93", {"start": v(31.09, 31.74) * mm, "end": v(33.09, 31.74) * mm});
            skArc(sketch, "E32.1.0.94", {"start": v(52.09, 31.74) * mm, "mid": v(51.38, 31.45) * mm, "end": v(51.09, 30.74) * mm});
            skLineSegment(sketch, "E32.1.0.95", {"start": v(38.09, 31.74) * mm, "end": v(40.09, 31.74) * mm});
            skArc(sketch, "E32.1.0.96", {"start": v(59.09, 31.74) * mm, "mid": v(58.38, 31.45) * mm, "end": v(58.09, 30.74) * mm});
            skArc(sketch, "E32.1.0.97", {"start": v(97.09, 30.74) * mm, "mid": v(96.8, 31.45) * mm, "end": v(96.09, 31.74) * mm});
            skLineSegment(sketch, "E32.1.0.98", {"start": v(59.09, 31.74) * mm, "end": v(61.09, 31.74) * mm});
            skArc(sketch, "E32.1.0.99", {"start": v(69.09, 30.74) * mm, "mid": v(68.8, 31.45) * mm, "end": v(68.09, 31.74) * mm});
            skLineSegment(sketch, "E32.1.0.100", {"start": v(94.09, 31.74) * mm, "end": v(96.09, 31.74) * mm});
            skLineSegment(sketch, "E32.1.0.101", {"start": v(24.09, 31.74) * mm, "end": v(26.09, 31.74) * mm});
            skArc(sketch, "E32.1.0.102", {"start": v(79.09, 24.74) * mm, "mid": v(79.38, 24.03) * mm, "end": v(80.09, 23.74) * mm});
            skArc(sketch, "E32.1.0.103", {"start": v(48.09, 30.74) * mm, "mid": v(47.8, 31.45) * mm, "end": v(47.09, 31.74) * mm});
            skLineSegment(sketch, "E32.1.0.104", {"start": v(73.09, 31.74) * mm, "end": v(75.09, 31.74) * mm});
            skArc(sketch, "E32.1.0.105", {"start": v(45.09, 31.74) * mm, "mid": v(44.38, 31.45) * mm, "end": v(44.09, 30.74) * mm});
            skArc(sketch, "E32.1.0.106", {"start": v(80.09, 31.74) * mm, "mid": v(79.38, 31.45) * mm, "end": v(79.09, 30.74) * mm});
            skLineSegment(sketch, "E32.1.0.107", {"start": v(93.09, 23.74) * mm, "end": v(96.09, 23.74) * mm, "construction": true});
            skLineSegment(sketch, "E32.1.0.108", {"start": v(72.09, 23.74) * mm, "end": v(75.09, 23.74) * mm, "construction": true});
            skArc(sketch, "E32.1.0.109", {"start": v(93.09, 24.74) * mm, "mid": v(93.38, 24.03) * mm, "end": v(94.09, 23.74) * mm});
            skArc(sketch, "E32.1.0.110", {"start": v(44.09, 24.74) * mm, "mid": v(44.38, 24.03) * mm, "end": v(45.09, 23.74) * mm});
            skArc(sketch, "E32.1.0.111", {"start": v(89.09, 23.74) * mm, "mid": v(89.8, 24.03) * mm, "end": v(90.09, 24.74) * mm});
            skLineSegment(sketch, "E32.1.0.112", {"start": v(73.09, 23.74) * mm, "end": v(75.09, 23.74) * mm});
            skArc(sketch, "E32.1.0.113", {"start": v(86.09, 24.74) * mm, "mid": v(86.38, 24.03) * mm, "end": v(87.09, 23.74) * mm});
            skArc(sketch, "E32.1.0.114", {"start": v(82.09, 23.74) * mm, "mid": v(82.8, 24.03) * mm, "end": v(83.09, 24.74) * mm});
            skLineSegment(sketch, "E32.1.0.115", {"start": v(23.09, 23.74) * mm, "end": v(26.09, 23.74) * mm, "construction": true});
            skArc(sketch, "E32.1.0.116", {"start": v(37.09, 24.74) * mm, "mid": v(37.38, 24.03) * mm, "end": v(38.09, 23.74) * mm});
            skLineSegment(sketch, "E32.1.0.117", {"start": v(80.09, 23.74) * mm, "end": v(82.09, 23.74) * mm});
            skArc(sketch, "E32.1.0.118", {"start": v(23.09, 24.74) * mm, "mid": v(23.38, 24.03) * mm, "end": v(24.09, 23.74) * mm});
            skArc(sketch, "E32.1.0.119", {"start": v(75.09, 23.74) * mm, "mid": v(75.8, 24.03) * mm, "end": v(76.09, 24.74) * mm});
            skArc(sketch, "E32.1.0.120", {"start": v(26.09, 23.74) * mm, "mid": v(26.8, 24.03) * mm, "end": v(27.09, 24.74) * mm});
            skLineSegment(sketch, "E32.1.0.121", {"start": v(51.09, 23.74) * mm, "end": v(54.09, 23.74) * mm, "construction": true});
            skArc(sketch, "E32.1.0.122", {"start": v(72.09, 24.74) * mm, "mid": v(72.38, 24.03) * mm, "end": v(73.09, 23.74) * mm});
            skArc(sketch, "E32.1.0.123", {"start": v(61.09, 23.74) * mm, "mid": v(61.8, 24.03) * mm, "end": v(62.09, 24.74) * mm});
            skLineSegment(sketch, "E32.1.0.124", {"start": v(87.09, 23.74) * mm, "end": v(89.09, 23.74) * mm});
            skLineSegment(sketch, "E32.1.0.125", {"start": v(37.09, 23.74) * mm, "end": v(40.09, 23.74) * mm, "construction": true});
            skLineSegment(sketch, "E32.1.0.126", {"start": v(45.09, 23.74) * mm, "end": v(47.09, 23.74) * mm});
            skLineSegment(sketch, "E32.1.0.127", {"start": v(86.09, 23.74) * mm, "end": v(89.09, 23.74) * mm, "construction": true});
            skArc(sketch, "E32.1.0.128", {"start": v(40.09, 23.74) * mm, "mid": v(40.8, 24.03) * mm, "end": v(41.09, 24.74) * mm});
            skLineSegment(sketch, "E32.1.0.129", {"start": v(94.09, 23.74) * mm, "end": v(96.09, 23.74) * mm});
            skArc(sketch, "E32.1.0.130", {"start": v(47.09, 23.74) * mm, "mid": v(47.8, 24.03) * mm, "end": v(48.09, 24.74) * mm});
            skArc(sketch, "E32.1.0.131", {"start": v(96.09, 23.74) * mm, "mid": v(96.8, 24.03) * mm, "end": v(97.09, 24.74) * mm});
            skArc(sketch, "E32.1.0.132", {"start": v(33.09, 23.74) * mm, "mid": v(33.8, 24.03) * mm, "end": v(34.09, 24.74) * mm});
            skArc(sketch, "E32.1.0.133", {"start": v(68.09, 23.74) * mm, "mid": v(68.8, 24.03) * mm, "end": v(69.09, 24.74) * mm});
            skArc(sketch, "E32.1.0.134", {"start": v(54.09, 23.74) * mm, "mid": v(54.8, 24.03) * mm, "end": v(55.09, 24.74) * mm});
            skLineSegment(sketch, "E32.1.0.135", {"start": v(30.09, 23.74) * mm, "end": v(33.09, 23.74) * mm, "construction": true});
            skLineSegment(sketch, "E32.1.0.136", {"start": v(38.09, 23.74) * mm, "end": v(40.09, 23.74) * mm});
            skArc(sketch, "E32.1.0.137", {"start": v(51.09, 24.74) * mm, "mid": v(51.38, 24.03) * mm, "end": v(52.09, 23.74) * mm});
            skLineSegment(sketch, "E32.1.0.138", {"start": v(44.09, 23.74) * mm, "end": v(47.09, 23.74) * mm, "construction": true});
            skLineSegment(sketch, "E32.1.0.139", {"start": v(66.09, 23.74) * mm, "end": v(68.09, 23.74) * mm});
            skArc(sketch, "E32.1.0.140", {"start": v(30.09, 24.74) * mm, "mid": v(30.38, 24.03) * mm, "end": v(31.09, 23.74) * mm});
            skLineSegment(sketch, "E32.1.0.141", {"start": v(24.09, 23.74) * mm, "end": v(26.09, 23.74) * mm});
            skLineSegment(sketch, "E32.1.0.142", {"start": v(31.09, 23.74) * mm, "end": v(33.09, 23.74) * mm});
            skLineSegment(sketch, "E32.1.0.143", {"start": v(52.09, 23.74) * mm, "end": v(54.09, 23.74) * mm});
            skPoint(sketch, "E32.2.0.0", {"position": v(97.03, 12.74) * mm});
            skPoint(sketch, "E32.2.0.1", {"position": v(44.03, 20.74) * mm});
            skPoint(sketch, "E32.2.0.2", {"position": v(30.03, 20.74) * mm});
            skLineSegment(sketch, "E32.2.0.3", {"start": v(34.03, 19.74) * mm, "end": v(34.03, 13.74) * mm});
            skPoint(sketch, "E32.2.0.4", {"position": v(41.03, 20.74) * mm});
            skPoint(sketch, "E32.2.0.5", {"position": v(37.03, 20.74) * mm});
            skPoint(sketch, "E32.2.0.6", {"position": v(27.03, 12.74) * mm});
            skLineSegment(sketch, "E32.2.0.7", {"start": v(93.03, 19.74) * mm, "end": v(93.03, 13.74) * mm});
            skPoint(sketch, "E32.2.0.8", {"position": v(76.03, 20.74) * mm});
            skPoint(sketch, "E32.2.0.9", {"position": v(86.03, 20.74) * mm});
            skLineSegment(sketch, "E32.2.0.10", {"start": v(79.03, 19.74) * mm, "end": v(79.03, 13.74) * mm});
            skPoint(sketch, "E32.2.0.11", {"position": v(27.03, 20.74) * mm});
            skPoint(sketch, "E32.2.0.12", {"position": v(72.03, 20.74) * mm});
            skLineSegment(sketch, "E32.2.0.13", {"start": v(69.03, 19.74) * mm, "end": v(69.03, 13.74) * mm});
            skLineSegment(sketch, "E32.2.0.14", {"start": v(76.03, 19.74) * mm, "end": v(76.03, 13.74) * mm});
            skPoint(sketch, "E32.2.0.15", {"position": v(58.03, 20.74) * mm});
            skPoint(sketch, "E32.2.0.16", {"position": v(41.03, 12.74) * mm});
            skPoint(sketch, "E32.2.0.17", {"position": v(55.03, 20.74) * mm});
            skPoint(sketch, "E32.2.0.18", {"position": v(69.03, 20.74) * mm});
            skPoint(sketch, "E32.2.0.19", {"position": v(83.03, 20.74) * mm});
            skPoint(sketch, "E32.2.0.20", {"position": v(69.03, 12.74) * mm});
            skPoint(sketch, "E32.2.0.21", {"position": v(97.03, 20.74) * mm});
            skLineSegment(sketch, "E32.2.0.22", {"start": v(51.03, 19.74) * mm, "end": v(51.03, 13.74) * mm});
            skLineSegment(sketch, "E32.2.0.23", {"start": v(55.03, 19.74) * mm, "end": v(55.03, 13.74) * mm});
            skLineSegment(sketch, "E32.2.0.24", {"start": v(37.03, 19.74) * mm, "end": v(37.03, 13.74) * mm});
            skLineSegment(sketch, "E32.2.0.25", {"start": v(44.03, 19.74) * mm, "end": v(44.03, 13.74) * mm});
            skLineSegment(sketch, "E32.2.0.26", {"start": v(86.03, 19.74) * mm, "end": v(86.03, 13.74) * mm});
            skLineSegment(sketch, "E32.2.0.27", {"start": v(41.03, 19.74) * mm, "end": v(41.03, 13.74) * mm});
            skLineSegment(sketch, "E32.2.0.28", {"start": v(65.03, 19.74) * mm, "end": v(65.03, 13.74) * mm});
            skLineSegment(sketch, "E32.2.0.29", {"start": v(90.03, 19.74) * mm, "end": v(90.03, 13.74) * mm});
            skLineSegment(sketch, "E32.2.0.30", {"start": v(27.03, 19.74) * mm, "end": v(27.03, 13.74) * mm});
            skPoint(sketch, "E32.2.0.31", {"position": v(76.03, 12.74) * mm});
            skPoint(sketch, "E32.2.0.32", {"position": v(90.03, 12.74) * mm});
            skPoint(sketch, "E32.2.0.33", {"position": v(34.03, 12.74) * mm});
            skPoint(sketch, "E32.2.0.34", {"position": v(48.03, 12.74) * mm});
            skPoint(sketch, "E32.2.0.35", {"position": v(62.03, 12.74) * mm});
            skPoint(sketch, "E32.2.0.36", {"position": v(83.03, 12.74) * mm});
            skLineSegment(sketch, "E32.2.0.37", {"start": v(72.03, 19.74) * mm, "end": v(72.03, 13.74) * mm});
            skLineSegment(sketch, "E32.2.0.38", {"start": v(23.03, 19.74) * mm, "end": v(23.03, 13.74) * mm});
            skPoint(sketch, "E32.2.0.39", {"position": v(72.03, 12.74) * mm});
            skPoint(sketch, "E32.2.0.40", {"position": v(86.03, 12.74) * mm});
            skPoint(sketch, "E32.2.0.41", {"position": v(30.03, 12.74) * mm});
            skPoint(sketch, "E32.2.0.42", {"position": v(44.03, 12.74) * mm});
            skPoint(sketch, "E32.2.0.43", {"position": v(58.03, 12.74) * mm});
            skPoint(sketch, "E32.2.0.44", {"position": v(90.03, 20.74) * mm});
            skPoint(sketch, "E32.2.0.45", {"position": v(51.03, 20.74) * mm});
            skPoint(sketch, "E32.2.0.46", {"position": v(55.03, 12.74) * mm});
            skPoint(sketch, "E32.2.0.47", {"position": v(34.03, 20.74) * mm});
            skLineSegment(sketch, "E32.2.0.48", {"start": v(97.03, 19.74) * mm, "end": v(97.03, 13.74) * mm});
            skPoint(sketch, "E32.2.0.49", {"position": v(23.03, 12.74) * mm});
            skLineSegment(sketch, "E32.2.0.50", {"start": v(48.03, 19.74) * mm, "end": v(48.03, 13.74) * mm});
            skPoint(sketch, "E32.2.0.51", {"position": v(65.03, 20.74) * mm});
            skLineSegment(sketch, "E32.2.0.52", {"start": v(83.03, 19.74) * mm, "end": v(83.03, 13.74) * mm});
            skPoint(sketch, "E32.2.0.53", {"position": v(79.03, 20.74) * mm});
            skPoint(sketch, "E32.2.0.54", {"position": v(48.03, 20.74) * mm});
            skPoint(sketch, "E32.2.0.55", {"position": v(62.03, 20.74) * mm});
            skLineSegment(sketch, "E32.2.0.56", {"start": v(62.03, 19.74) * mm, "end": v(62.03, 13.74) * mm});
            skPoint(sketch, "E32.2.0.57", {"position": v(51.03, 12.74) * mm});
            skLineSegment(sketch, "E32.2.0.58", {"start": v(30.03, 19.74) * mm, "end": v(30.03, 13.74) * mm});
            skPoint(sketch, "E32.2.0.59", {"position": v(93.03, 20.74) * mm});
            skPoint(sketch, "E32.2.0.60", {"position": v(65.03, 12.74) * mm});
            skPoint(sketch, "E32.2.0.61", {"position": v(79.03, 12.74) * mm});
            skPoint(sketch, "E32.2.0.62", {"position": v(93.03, 12.74) * mm});
            skPoint(sketch, "E32.2.0.63", {"position": v(23.03, 20.74) * mm});
            skPoint(sketch, "E32.2.0.64", {"position": v(37.03, 12.74) * mm});
            skLineSegment(sketch, "E32.2.0.65", {"start": v(58.03, 19.74) * mm, "end": v(58.03, 13.74) * mm});
            skLineSegment(sketch, "E32.2.0.66", {"start": v(23.03, 12.74) * mm, "end": v(30.03, 12.74) * mm, "construction": true});
            skArc(sketch, "E32.2.0.67", {"start": v(66.03, 20.74) * mm, "mid": v(65.32, 20.45) * mm, "end": v(65.03, 19.74) * mm});
            skArc(sketch, "E32.2.0.68", {"start": v(83.03, 19.74) * mm, "mid": v(82.73, 20.45) * mm, "end": v(82.03, 20.74) * mm});
            skArc(sketch, "E32.2.0.69", {"start": v(65.03, 13.74) * mm, "mid": v(65.32, 13.03) * mm, "end": v(66.03, 12.74) * mm});
            skLineSegment(sketch, "E32.2.0.70", {"start": v(45.03, 20.74) * mm, "end": v(47.03, 20.74) * mm});
            skArc(sketch, "E32.2.0.71", {"start": v(94.03, 20.74) * mm, "mid": v(93.32, 20.45) * mm, "end": v(93.03, 19.74) * mm});
            skLineSegment(sketch, "E32.2.0.72", {"start": v(80.03, 20.74) * mm, "end": v(82.03, 20.74) * mm});
            skLineSegment(sketch, "E32.2.0.73", {"start": v(65.03, 12.74) * mm, "end": v(68.03, 12.74) * mm, "construction": true});
            skArc(sketch, "E32.2.0.74", {"start": v(62.03, 19.74) * mm, "mid": v(61.73, 20.45) * mm, "end": v(61.03, 20.74) * mm});
            skLineSegment(sketch, "E32.2.0.75", {"start": v(87.03, 20.74) * mm, "end": v(89.03, 20.74) * mm});
            skArc(sketch, "E32.2.0.76", {"start": v(55.03, 19.74) * mm, "mid": v(54.73, 20.45) * mm, "end": v(54.03, 20.74) * mm});
            skArc(sketch, "E32.2.0.77", {"start": v(34.03, 19.74) * mm, "mid": v(33.73, 20.45) * mm, "end": v(33.03, 20.74) * mm});
            skArc(sketch, "E32.2.0.78", {"start": v(38.03, 20.74) * mm, "mid": v(37.32, 20.45) * mm, "end": v(37.03, 19.74) * mm});
            skArc(sketch, "E32.2.0.79", {"start": v(87.03, 20.74) * mm, "mid": v(86.32, 20.45) * mm, "end": v(86.03, 19.74) * mm});
            skArc(sketch, "E32.2.0.80", {"start": v(41.03, 19.74) * mm, "mid": v(40.73, 20.45) * mm, "end": v(40.03, 20.74) * mm});
            skLineSegment(sketch, "E32.2.0.81", {"start": v(66.03, 20.74) * mm, "end": v(68.03, 20.74) * mm});
            skArc(sketch, "E32.2.0.82", {"start": v(31.03, 20.74) * mm, "mid": v(30.32, 20.45) * mm, "end": v(30.03, 19.74) * mm});
            skArc(sketch, "E32.2.0.83", {"start": v(90.03, 19.74) * mm, "mid": v(89.73, 20.45) * mm, "end": v(89.03, 20.74) * mm});
            skLineSegment(sketch, "E32.2.0.84", {"start": v(59.03, 12.74) * mm, "end": v(61.03, 12.74) * mm});
            skArc(sketch, "E32.2.0.85", {"start": v(24.03, 20.74) * mm, "mid": v(23.32, 20.45) * mm, "end": v(23.03, 19.74) * mm});
            skLineSegment(sketch, "E32.2.0.86", {"start": v(58.03, 12.74) * mm, "end": v(61.03, 12.74) * mm, "construction": true});
            skLineSegment(sketch, "E32.2.0.87", {"start": v(52.03, 20.74) * mm, "end": v(54.03, 20.74) * mm});
            skArc(sketch, "E32.2.0.88", {"start": v(73.03, 20.74) * mm, "mid": v(72.32, 20.45) * mm, "end": v(72.03, 19.74) * mm});
            skArc(sketch, "E32.2.0.89", {"start": v(27.03, 19.74) * mm, "mid": v(26.73, 20.45) * mm, "end": v(26.03, 20.74) * mm});
            skLineSegment(sketch, "E32.2.0.90", {"start": v(79.03, 12.74) * mm, "end": v(82.03, 12.74) * mm, "construction": true});
            skArc(sketch, "E32.2.0.91", {"start": v(58.03, 13.74) * mm, "mid": v(58.32, 13.03) * mm, "end": v(59.03, 12.74) * mm});
            skArc(sketch, "E32.2.0.92", {"start": v(76.03, 19.74) * mm, "mid": v(75.73, 20.45) * mm, "end": v(75.03, 20.74) * mm});
            skLineSegment(sketch, "E32.2.0.93", {"start": v(31.03, 20.74) * mm, "end": v(33.03, 20.74) * mm});
            skArc(sketch, "E32.2.0.94", {"start": v(52.03, 20.74) * mm, "mid": v(51.32, 20.45) * mm, "end": v(51.03, 19.74) * mm});
            skLineSegment(sketch, "E32.2.0.95", {"start": v(38.03, 20.74) * mm, "end": v(40.03, 20.74) * mm});
            skArc(sketch, "E32.2.0.96", {"start": v(59.03, 20.74) * mm, "mid": v(58.32, 20.45) * mm, "end": v(58.03, 19.74) * mm});
            skArc(sketch, "E32.2.0.97", {"start": v(97.03, 19.74) * mm, "mid": v(96.73, 20.45) * mm, "end": v(96.03, 20.74) * mm});
            skLineSegment(sketch, "E32.2.0.98", {"start": v(59.03, 20.74) * mm, "end": v(61.03, 20.74) * mm});
            skArc(sketch, "E32.2.0.99", {"start": v(69.03, 19.74) * mm, "mid": v(68.73, 20.45) * mm, "end": v(68.03, 20.74) * mm});
            skLineSegment(sketch, "E32.2.0.100", {"start": v(94.03, 20.74) * mm, "end": v(96.03, 20.74) * mm});
            skLineSegment(sketch, "E32.2.0.101", {"start": v(24.03, 20.74) * mm, "end": v(26.03, 20.74) * mm});
            skArc(sketch, "E32.2.0.102", {"start": v(79.03, 13.74) * mm, "mid": v(79.32, 13.03) * mm, "end": v(80.03, 12.74) * mm});
            skArc(sketch, "E32.2.0.103", {"start": v(48.03, 19.74) * mm, "mid": v(47.73, 20.45) * mm, "end": v(47.03, 20.74) * mm});
            skLineSegment(sketch, "E32.2.0.104", {"start": v(73.03, 20.74) * mm, "end": v(75.03, 20.74) * mm});
            skArc(sketch, "E32.2.0.105", {"start": v(45.03, 20.74) * mm, "mid": v(44.32, 20.45) * mm, "end": v(44.03, 19.74) * mm});
            skArc(sketch, "E32.2.0.106", {"start": v(80.03, 20.74) * mm, "mid": v(79.32, 20.45) * mm, "end": v(79.03, 19.74) * mm});
            skLineSegment(sketch, "E32.2.0.107", {"start": v(93.03, 12.74) * mm, "end": v(96.03, 12.74) * mm, "construction": true});
            skLineSegment(sketch, "E32.2.0.108", {"start": v(72.03, 12.74) * mm, "end": v(75.03, 12.74) * mm, "construction": true});
            skArc(sketch, "E32.2.0.109", {"start": v(93.03, 13.74) * mm, "mid": v(93.32, 13.03) * mm, "end": v(94.03, 12.74) * mm});
            skArc(sketch, "E32.2.0.110", {"start": v(44.03, 13.74) * mm, "mid": v(44.32, 13.03) * mm, "end": v(45.03, 12.74) * mm});
            skArc(sketch, "E32.2.0.111", {"start": v(89.03, 12.74) * mm, "mid": v(89.73, 13.03) * mm, "end": v(90.03, 13.74) * mm});
            skLineSegment(sketch, "E32.2.0.112", {"start": v(73.03, 12.74) * mm, "end": v(75.03, 12.74) * mm});
            skArc(sketch, "E32.2.0.113", {"start": v(86.03, 13.74) * mm, "mid": v(86.32, 13.03) * mm, "end": v(87.03, 12.74) * mm});
            skArc(sketch, "E32.2.0.114", {"start": v(82.03, 12.74) * mm, "mid": v(82.73, 13.03) * mm, "end": v(83.03, 13.74) * mm});
            skLineSegment(sketch, "E32.2.0.115", {"start": v(23.03, 12.74) * mm, "end": v(26.03, 12.74) * mm, "construction": true});
            skArc(sketch, "E32.2.0.116", {"start": v(37.03, 13.74) * mm, "mid": v(37.32, 13.03) * mm, "end": v(38.03, 12.74) * mm});
            skLineSegment(sketch, "E32.2.0.117", {"start": v(80.03, 12.74) * mm, "end": v(82.03, 12.74) * mm});
            skArc(sketch, "E32.2.0.118", {"start": v(23.03, 13.74) * mm, "mid": v(23.32, 13.03) * mm, "end": v(24.03, 12.74) * mm});
            skArc(sketch, "E32.2.0.119", {"start": v(75.03, 12.74) * mm, "mid": v(75.73, 13.03) * mm, "end": v(76.03, 13.74) * mm});
            skArc(sketch, "E32.2.0.120", {"start": v(26.03, 12.74) * mm, "mid": v(26.73, 13.03) * mm, "end": v(27.03, 13.74) * mm});
            skLineSegment(sketch, "E32.2.0.121", {"start": v(51.03, 12.74) * mm, "end": v(54.03, 12.74) * mm, "construction": true});
            skArc(sketch, "E32.2.0.122", {"start": v(72.03, 13.74) * mm, "mid": v(72.32, 13.03) * mm, "end": v(73.03, 12.74) * mm});
            skArc(sketch, "E32.2.0.123", {"start": v(61.03, 12.74) * mm, "mid": v(61.73, 13.03) * mm, "end": v(62.03, 13.74) * mm});
            skLineSegment(sketch, "E32.2.0.124", {"start": v(87.03, 12.74) * mm, "end": v(89.03, 12.74) * mm});
            skLineSegment(sketch, "E32.2.0.125", {"start": v(37.03, 12.74) * mm, "end": v(40.03, 12.74) * mm, "construction": true});
            skLineSegment(sketch, "E32.2.0.126", {"start": v(45.03, 12.74) * mm, "end": v(47.03, 12.74) * mm});
            skLineSegment(sketch, "E32.2.0.127", {"start": v(86.03, 12.74) * mm, "end": v(89.03, 12.74) * mm, "construction": true});
            skArc(sketch, "E32.2.0.128", {"start": v(40.03, 12.74) * mm, "mid": v(40.73, 13.03) * mm, "end": v(41.03, 13.74) * mm});
            skLineSegment(sketch, "E32.2.0.129", {"start": v(94.03, 12.74) * mm, "end": v(96.03, 12.74) * mm});
            skArc(sketch, "E32.2.0.130", {"start": v(47.03, 12.74) * mm, "mid": v(47.73, 13.03) * mm, "end": v(48.03, 13.74) * mm});
            skArc(sketch, "E32.2.0.131", {"start": v(96.03, 12.74) * mm, "mid": v(96.73, 13.03) * mm, "end": v(97.03, 13.74) * mm});
            skArc(sketch, "E32.2.0.132", {"start": v(33.03, 12.74) * mm, "mid": v(33.73, 13.03) * mm, "end": v(34.03, 13.74) * mm});
            skArc(sketch, "E32.2.0.133", {"start": v(68.03, 12.74) * mm, "mid": v(68.73, 13.03) * mm, "end": v(69.03, 13.74) * mm});
            skArc(sketch, "E32.2.0.134", {"start": v(54.03, 12.74) * mm, "mid": v(54.73, 13.03) * mm, "end": v(55.03, 13.74) * mm});
            skLineSegment(sketch, "E32.2.0.135", {"start": v(30.03, 12.74) * mm, "end": v(33.03, 12.74) * mm, "construction": true});
            skLineSegment(sketch, "E32.2.0.136", {"start": v(38.03, 12.74) * mm, "end": v(40.03, 12.74) * mm});
            skArc(sketch, "E32.2.0.137", {"start": v(51.03, 13.74) * mm, "mid": v(51.32, 13.03) * mm, "end": v(52.03, 12.74) * mm});
            skLineSegment(sketch, "E32.2.0.138", {"start": v(44.03, 12.74) * mm, "end": v(47.03, 12.74) * mm, "construction": true});
            skLineSegment(sketch, "E32.2.0.139", {"start": v(66.03, 12.74) * mm, "end": v(68.03, 12.74) * mm});
            skArc(sketch, "E32.2.0.140", {"start": v(30.03, 13.74) * mm, "mid": v(30.32, 13.03) * mm, "end": v(31.03, 12.74) * mm});
            skLineSegment(sketch, "E32.2.0.141", {"start": v(24.03, 12.74) * mm, "end": v(26.03, 12.74) * mm});
            skLineSegment(sketch, "E32.2.0.142", {"start": v(31.03, 12.74) * mm, "end": v(33.03, 12.74) * mm});
            skLineSegment(sketch, "E32.2.0.143", {"start": v(52.03, 12.74) * mm, "end": v(54.03, 12.74) * mm});
            skLineSegment(sketch, "E32.direction1", {"start": v(23.15, 34.74) * mm, "end": v(23.09, 23.74) * mm, "construction": true});
            skSolve(sketch);
        }
        {
            var Q0;
            Q0 = qSketchRegion(id + "F2", true);
            extrude(context, id + "F3", {"entities" : qUnion([Q0]), "operationType" : NewBodyOperationType.REMOVE, "oppositeDirection" : true, "depth" : 2 * mm, "offsetDistance" : 25 * mm});
        }
    });
